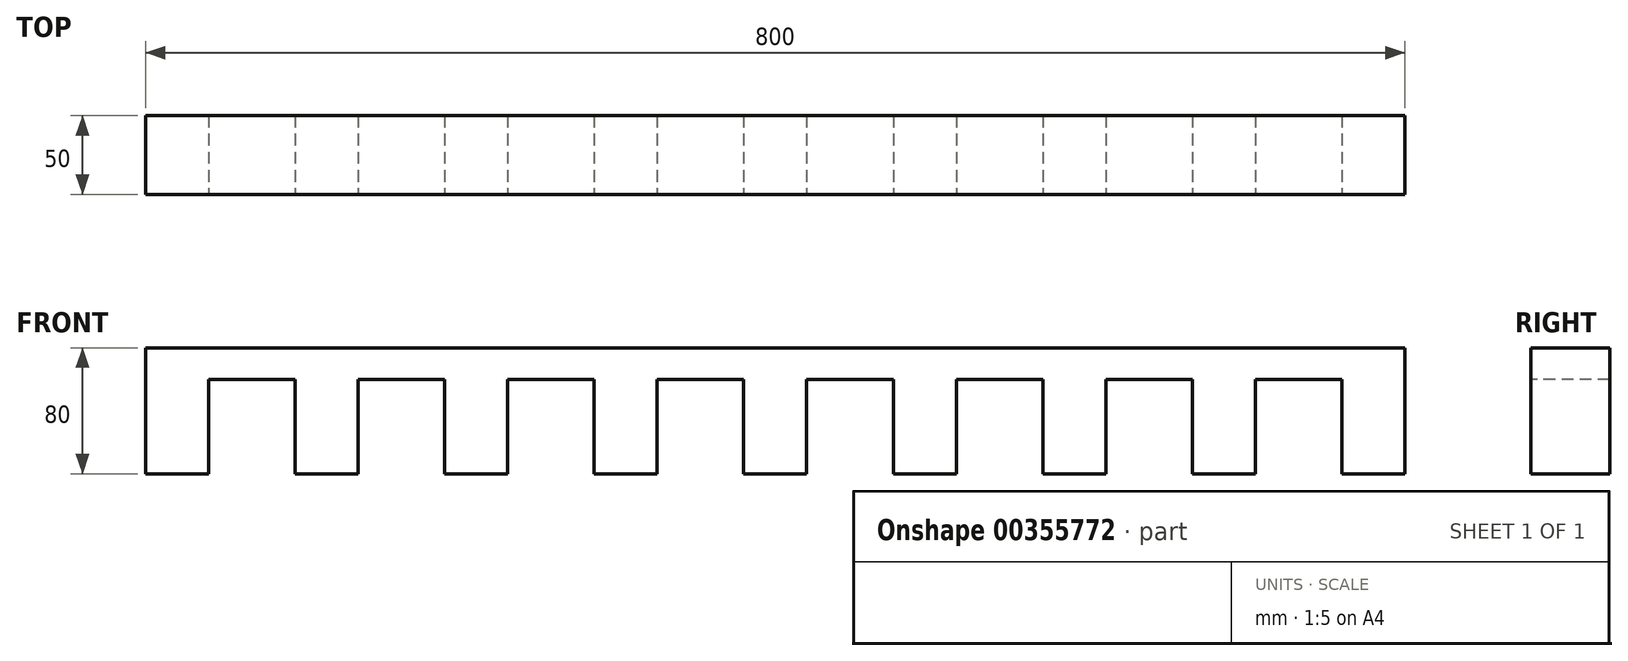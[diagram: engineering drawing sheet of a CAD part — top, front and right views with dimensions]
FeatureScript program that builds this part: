
annotation { "Feature Type Name" : "Feature", "Feature Type Description" : "" }
export const myFeature = defineFeature(function(context is Context, id is Id, definition is map)
    precondition{}
    {
        {
            var Q0;
            Q0=qCreatedBy(makeId("Front.planeOp"),FACE);
            var sketch = newSketch(context, id + "F0", { "sketchPlane" : qUnion([Q0])});
            skLineSegment(sketch, "E0.bottom", {"start": v(-404.78, 0) * mm, "end": v(395.22, 0) * mm});
            skLineSegment(sketch, "E0.top", {"start": v(-404.78, -80) * mm, "end": v(395.22, -80) * mm});
            skLineSegment(sketch, "E0.left", {"start": v(-404.78, 0) * mm, "end": v(-404.78, -80) * mm});
            skLineSegment(sketch, "E0.right", {"start": v(395.22, 0) * mm, "end": v(395.22, -80) * mm});
            skSolve(sketch);
        }
        {
            var Q0;
            Q0=makeQuery(id+"F0.imprint","IMPRINT",FACE,{"disambiguationData":[TD([[makeQuery(id+"F0.imprint","IMPRINT",EDGE,{"derivedFrom":sQuery(id+"F0.wireOp",EDGE,"E0.bottom")}),-1.0]])]});
            extrude(context, id + "F1", {"entities" : qUnion([Q0]), "depth" : 50 * mm});
        }
        {
            var Q0;
            Q0=makeQuery(id+"F1.opExtrude","CAP_FACE",FACE,{"disambiguationData":[OSD([sQuery(id+"F0.wireOp",EDGE,"E0.bottom"),sQuery(id+"F0.wireOp",EDGE,"E0.top"),sQuery(id+"F0.wireOp",EDGE,"E0.left"),sQuery(id+"F0.wireOp",EDGE,"E0.right")])],"isStart":false});
            var sketch = newSketch(context, id + "F2", { "sketchPlane" : qUnion([Q0])});
            skLineSegment(sketch, "E1.bottom", {"start": v(-364.78, -80) * mm, "end": v(-309.78, -80) * mm});
            skLineSegment(sketch, "E1.top", {"start": v(-364.78, -20) * mm, "end": v(-309.78, -20) * mm});
            skLineSegment(sketch, "E1.left", {"start": v(-364.78, -80) * mm, "end": v(-364.78, -20) * mm});
            skLineSegment(sketch, "E1.right", {"start": v(-309.78, -80) * mm, "end": v(-309.78, -20) * mm});
            skLineSegment(sketch, "E2.bottom", {"start": v(-269.78, -80) * mm, "end": v(-214.78, -80) * mm});
            skLineSegment(sketch, "E2.top", {"start": v(-269.78, -20) * mm, "end": v(-214.78, -20) * mm});
            skLineSegment(sketch, "E2.left", {"start": v(-269.78, -80) * mm, "end": v(-269.78, -20) * mm});
            skLineSegment(sketch, "E2.right", {"start": v(-214.78, -80) * mm, "end": v(-214.78, -20) * mm});
            skLineSegment(sketch, "E3.bottom", {"start": v(-174.78, -80) * mm, "end": v(-119.78, -80) * mm});
            skLineSegment(sketch, "E3.top", {"start": v(-174.78, -20) * mm, "end": v(-119.78, -20) * mm});
            skLineSegment(sketch, "E3.left", {"start": v(-174.78, -80) * mm, "end": v(-174.78, -20) * mm});
            skLineSegment(sketch, "E3.right", {"start": v(-119.78, -80) * mm, "end": v(-119.78, -20) * mm});
            skPoint(sketch, "E4.oppositeSnap0", {"position": v(-147.28, -20) * mm});
            skLineSegment(sketch, "E4.bottom", {"start": v(-79.78, -80) * mm, "end": v(-24.78, -80) * mm});
            skLineSegment(sketch, "E4.top", {"start": v(-79.78, -20) * mm, "end": v(-24.78, -20) * mm});
            skLineSegment(sketch, "E4.left", {"start": v(-79.78, -80) * mm, "end": v(-79.78, -20) * mm});
            skLineSegment(sketch, "E4.right", {"start": v(-24.78, -80) * mm, "end": v(-24.78, -20) * mm});
            skLineSegment(sketch, "E5.bottom", {"start": v(15.22, -80) * mm, "end": v(70.22, -80) * mm});
            skLineSegment(sketch, "E5.top", {"start": v(15.22, -20) * mm, "end": v(70.22, -20) * mm});
            skLineSegment(sketch, "E5.left", {"start": v(15.22, -80) * mm, "end": v(15.22, -20) * mm});
            skLineSegment(sketch, "E5.right", {"start": v(70.22, -80) * mm, "end": v(70.22, -20) * mm});
            skLineSegment(sketch, "E6.bottom", {"start": v(110.22, -80) * mm, "end": v(165.22, -80) * mm});
            skLineSegment(sketch, "E6.top", {"start": v(110.22, -20) * mm, "end": v(165.22, -20) * mm});
            skLineSegment(sketch, "E6.left", {"start": v(110.22, -80) * mm, "end": v(110.22, -20) * mm});
            skLineSegment(sketch, "E6.right", {"start": v(165.22, -80) * mm, "end": v(165.22, -20) * mm});
            skLineSegment(sketch, "E7.bottom", {"start": v(205.22, -80) * mm, "end": v(260.22, -80) * mm});
            skLineSegment(sketch, "E7.top", {"start": v(205.22, -20) * mm, "end": v(260.22, -20) * mm});
            skLineSegment(sketch, "E7.left", {"start": v(205.22, -80) * mm, "end": v(205.22, -20) * mm});
            skLineSegment(sketch, "E7.right", {"start": v(260.22, -80) * mm, "end": v(260.22, -20) * mm});
            skLineSegment(sketch, "E8.bottom", {"start": v(300.22, -80) * mm, "end": v(355.22, -80) * mm});
            skLineSegment(sketch, "E8.top", {"start": v(300.22, -20) * mm, "end": v(355.22, -20) * mm});
            skLineSegment(sketch, "E8.left", {"start": v(300.22, -80) * mm, "end": v(300.22, -20) * mm});
            skLineSegment(sketch, "E8.right", {"start": v(355.22, -80) * mm, "end": v(355.22, -20) * mm});
            skSolve(sketch);
        }
        {
            var Q0;
            Q0=qSketchRegion(id+"F2",true);
            extrude(context, id + "F3", {"entities" : qUnion([Q0]), "operationType" : NewBodyOperationType.REMOVE, "oppositeDirection" : true, "depth" : 50 * mm});
        }
    });
